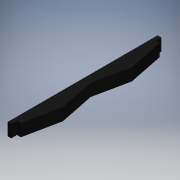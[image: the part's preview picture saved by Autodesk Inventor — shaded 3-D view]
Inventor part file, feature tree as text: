
AUTODESK INVENTOR PART (.ipt)
format: ipt  version: 2017 (Build 210142000, 142)  size: 118,784 bytes
history: native  units: in
note: dims shown in document units (in); Inventor stores cm internally (conversion verified against a paired STEP export)
features: extrude x3, sketch x3
ambient origin geometry x8: Origin, YZ Plane, XZ Plane, XY Plane, X Axis, Y Axis, Z Axis, Center Point
bodies: Solid1 (feature_tree)
feature tree (6):
  extrude  "Extrusion1"  Depth=0.134in
  sketch  "Sketch2"  dims[d2=0.134in d3=0.6115in]
  extrude  "Extrusion2"  Depth=0.134in
  extrude  "Extrusion3"  Depth=0.101in
  sketch  "Sketch1"  dims[d0=2.436in d1=0.134in]
  sketch  "Sketch3"  dims[d4=1.223in d5=0.6115in d6=0.125in d7=0.125in d8=0.2156in d9=0.0in d10=0.065in d11=0.065in d12=0.101in d13=0.0in d14=0.101in d15=0.0in]
